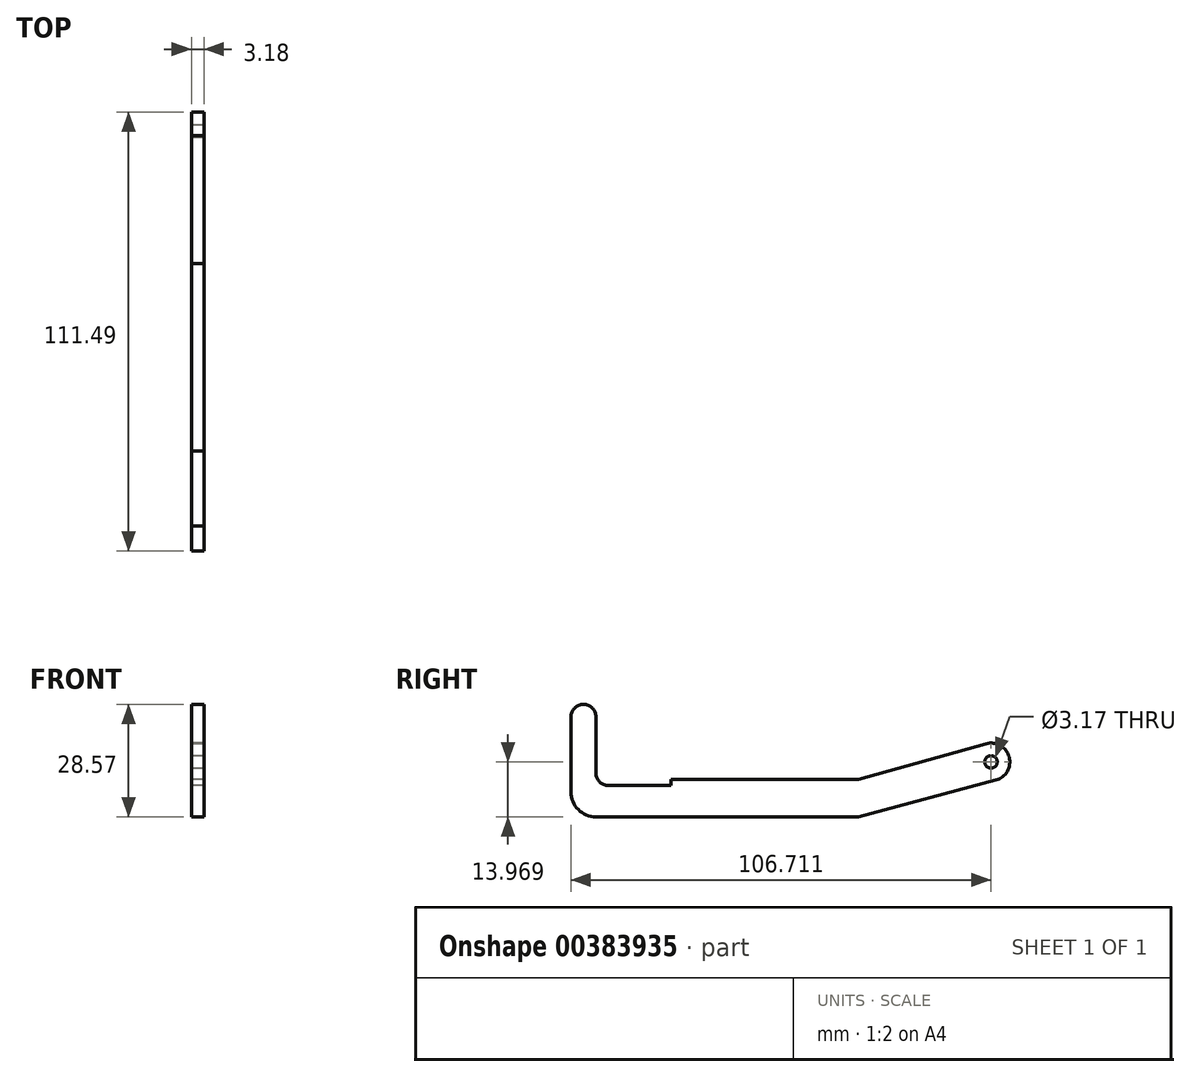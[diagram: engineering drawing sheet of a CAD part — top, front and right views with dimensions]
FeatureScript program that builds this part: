
annotation { "Feature Type Name" : "Feature", "Feature Type Description" : "" }
export const myFeature = defineFeature(function(context is Context, id is Id, definition is map)
    precondition{}
    {
        {
            var Q0;
            Q0=qCreatedBy(makeId("Right.planeOp"),FACE);
            var sketch = newSketch(context, id + "F0", { "sketchPlane" : qUnion([Q0])});
            skPoint(sketch, "E0.middle", {"position": v(-21.93, 27.71) * mm});
            skLineSegment(sketch, "E1", {"start": v(33.64, 48.35) * mm, "end": v(33.64, 34.06) * mm});
            skLineSegment(sketch, "E2", {"start": v(36.81, 30.89) * mm, "end": v(52.69, 30.89) * mm});
            skLineSegment(sketch, "E3", {"start": v(52.69, 30.89) * mm, "end": v(52.69, 32.47) * mm});
            skLineSegment(sketch, "E4", {"start": v(52.69, 32.47) * mm, "end": v(100.31, 32.47) * mm});
            skLineSegment(sketch, "E5", {"start": v(27.29, 48.35) * mm, "end": v(27.29, 29.3) * mm});
            skLineSegment(sketch, "E6", {"start": v(33.64, 22.95) * mm, "end": v(100.31, 22.95) * mm});
            skLineSegment(sketch, "E7", {"start": v(100.31, 22.95) * mm, "end": v(135.24, 32.3) * mm});
            skArc(sketch, "E8", {"start": v(135.24, 32.3) * mm, "mid": v(138.61, 38.16) * mm, "end": v(132.77, 41.53) * mm});
            skLineSegment(sketch, "E9", {"start": v(132.77, 41.53) * mm, "end": v(100.31, 32.47) * mm});
            skArc(sketch, "E10", {"start": v(33.64, 48.35) * mm, "mid": v(30.46, 51.52) * mm, "end": v(27.29, 48.35) * mm});
            skPoint(sketch, "E11.visualSharp", {"position": v(33.64, 30.89) * mm});
            skArc(sketch, "E11.filletArc", {"start": v(33.64, 34.06) * mm, "mid": v(34.57, 31.82) * mm, "end": v(36.81, 30.89) * mm});
            skPoint(sketch, "E12.visualSharp", {"position": v(27.29, 22.95) * mm});
            skArc(sketch, "E12.filletArc", {"start": v(27.29, 29.3) * mm, "mid": v(29.15, 24.8) * mm, "end": v(33.64, 22.95) * mm});
            skSolve(sketch);
        }
        {
            var Q0;
            Q0=qCreatedBy(makeId("Right.planeOp"),FACE);
            var sketch = newSketch(context, id + "F1", { "sketchPlane" : qUnion([Q0])});
            skCircle(sketch, "E13", {"center": v(134, 36.92) * mm, "radius": 1.59 * mm});
            skSolve(sketch);
        }
        {
            var Q0;
            Q0 = qSketchRegion(id + "F0", true);
            extrude(context, id + "F2", {"entities" : qUnion([Q0]), "endBound" : BoundingType.SYMMETRIC, "depth" : 3.17 * mm});
        }
        {
            var Q0;
            Q0 = qSketchRegion(id + "F1", true);
            extrude(context, id + "F3", {"entities" : qUnion([Q0]), "operationType" : NewBodyOperationType.REMOVE, "endBound" : BoundingType.SYMMETRIC, "oppositeDirection" : true, "depth" : 25.4 * mm});
        }
    });
